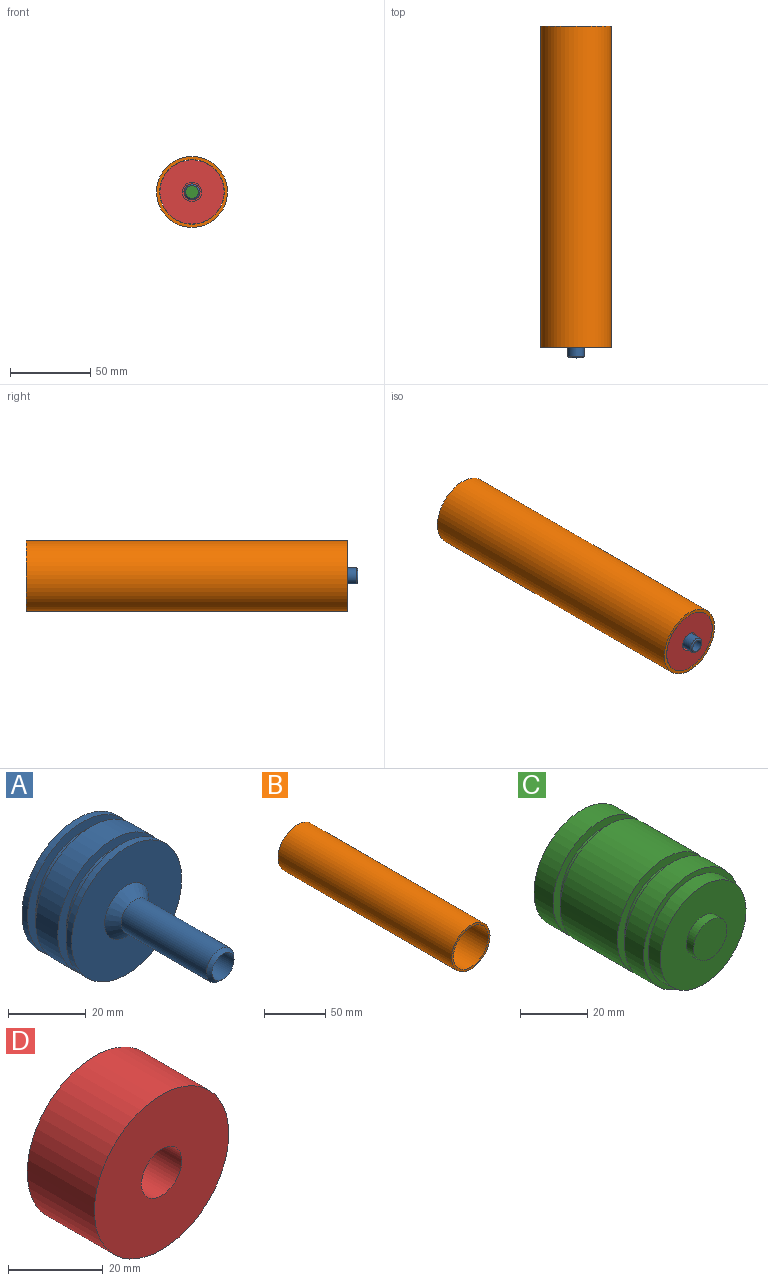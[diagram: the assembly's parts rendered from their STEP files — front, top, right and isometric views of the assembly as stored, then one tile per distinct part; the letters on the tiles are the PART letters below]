
ASSEMBLY  parts=4 mates=3
PART A: 19 faces, bbox 40x55x40 mm
  f0: plane 40x40mm, normal (0,1,0), area 452.4mm2, adj f1,f18
  f1: cylinder r=20mm len=40mm, axis (0,-1,0), area 251.3mm2, adj f0,f2
  f2: plane 40x40mm, normal (0,-1,0), area 348.7mm2, adj f1,f3
  f3: cylinder r=17mm len=34mm, axis (0,-1,0), area 320.4mm2, adj f2,f4
  f4: plane 40x40mm, normal (0,1,0), area 348.7mm2, adj f3,f5
  f5: cylinder r=20mm len=40mm, axis (0,-1,0), area 1005.3mm2, adj f4,f6
  f6: plane 40x40mm, normal (0,-1,0), area 348.7mm2, adj f5,f7
  f7: cylinder r=17mm len=34mm, axis (0,-1,0), area 320.4mm2, adj f6,f8
  f8: plane 40x40mm, normal (0,1,0), area 348.7mm2, adj f7,f9
  f9: cylinder r=20mm len=40mm, axis (0,-1,0), area 251.3mm2, adj f8,f10
  f10: plane 40x40mm, normal (0,-1,0), area 1055.6mm2, adj f9,f11
  f11: cone r=5mm half-angle=45deg, axis (0,1,0), area 173.3mm2, adj f10,f12
  f12: cylinder r=5mm len=31mm, axis (0,-1,0), area 973.9mm2, adj f11,f13
  f13: cone r=5mm half-angle=45deg, axis (0,1,0), area 40mm2, adj f12,f14
  f14: cylinder r=4mm len=45mm, axis (0,-1,0), area 1131mm2, adj f13,f15
  f15: cone r=12mm half-angle=45deg, axis (0,1,0), area 568.7mm2, adj f14,f16
  f16: cylinder r=12mm len=24mm, axis (0,-1,0), area 150.8mm2, adj f15,f17
  f17: plane 32x32mm, normal (0,1,0), area 351.9mm2, adj f16,f18
  f18: cylinder r=16mm len=32mm, axis (0,-1,0), area 201.1mm2, adj f0,f17
PART B: 4 faces, bbox 44.2x200x44.2 mm
  f0: cylinder r=22.1mm len=200mm, axis (0,-1,0), area 27771.7mm2, adj f1,f3
  f1: plane 44.2x44.2mm, normal (0,-1,0), area 265.2mm2, adj f0,f2
  f2: cylinder r=20.1mm len=200mm, axis (0,-1,0), area 25258.4mm2, adj f1,f3
  f3: plane 44.2x44.2mm, normal (0,1,0), area 265.2mm2, adj f0,f2
PART C: 15 faces, bbox 40x54x40 mm
  f0: plane 14x14mm, normal (0,-1,0), area 153.9mm2, adj f14
  f1: plane 40x40mm, normal (0,1,0), area 1256.6mm2, adj f2
  f2: cylinder r=20mm len=40mm, axis (0,-1,0), area 1005.3mm2, adj f1,f3
  f3: plane 40x40mm, normal (0,-1,0), area 348.7mm2, adj f2,f4
  f4: cylinder r=17mm len=34mm, axis (0,-1,0), area 320.4mm2, adj f3,f5
  f5: plane 40x40mm, normal (0,1,0), area 348.7mm2, adj f4,f6
  f6: cylinder r=20mm len=40mm, axis (0,-1,0), area 3015.9mm2, adj f5,f7
  f7: plane 40x40mm, normal (0,-1,0), area 348.7mm2, adj f6,f8
  f8: cylinder r=17mm len=34mm, axis (0,-1,0), area 320.4mm2, adj f7,f9
  f9: plane 40x40mm, normal (0,1,0), area 348.7mm2, adj f8,f10
  f10: cylinder r=20mm len=40mm, axis (0,-1,0), area 1005.3mm2, adj f9,f11
  f11: plane 40x40mm, normal (0,-1,0), area 238.8mm2, adj f10,f12
  f12: cylinder r=18mm len=36mm, axis (0,-1,0), area 565.5mm2, adj f11,f13
  f13: plane 36x36mm, normal (0,-1,0), area 863.9mm2, adj f12,f14
  f14: cylinder r=7mm len=14mm, axis (0,-1,0), area 131.9mm2, adj f0,f13
PART D: 7 faces, bbox 40x20x40 mm
  f0: cylinder r=20mm len=40mm, axis (0,-1,0), area 2513.3mm2, adj f1,f6
  f1: plane 40x40mm, normal (0,-1,0), area 1143.5mm2, adj f0,f2
  f2: cylinder r=6mm len=15.42mm, axis (0,-1,0), area 581.4mm2, adj f1,f3
  f3: plane 12x12mm, normal (0,-1,0), area 34.6mm2, adj f2,f4
  f4: cylinder r=5mm len=10mm, axis (0,-1,0), area 49.5mm2, adj f3,f5
  f5: cone r=5mm half-angle=45deg, axis (0,1,0), area 173.3mm2, adj f4,f6
  f6: plane 40x40mm, normal (0,1,0), area 1055.6mm2, adj f0,f5
PLACE A t=(-2.23,-65.63,10.38)mm
PLACE B t=(-2.23,1.27,10.38)mm
PLACE C t=(-2.23,-23.18,10.38)mm
PLACE D t=(-2.23,-84.74,10.38)mm
MATE slider C.f2 <-> B.f0  axis (0,-1,0) through (-2.23,-12.43,10.38)mm
MATE planar D.f0 <-> B.f0  axis (0,-1,0) through (-2.23,-93.83,10.38)mm
MATE slider A.f1 <-> B.f0  axis (0,-1,0) through (-2.23,-56.63,10.38)mm
